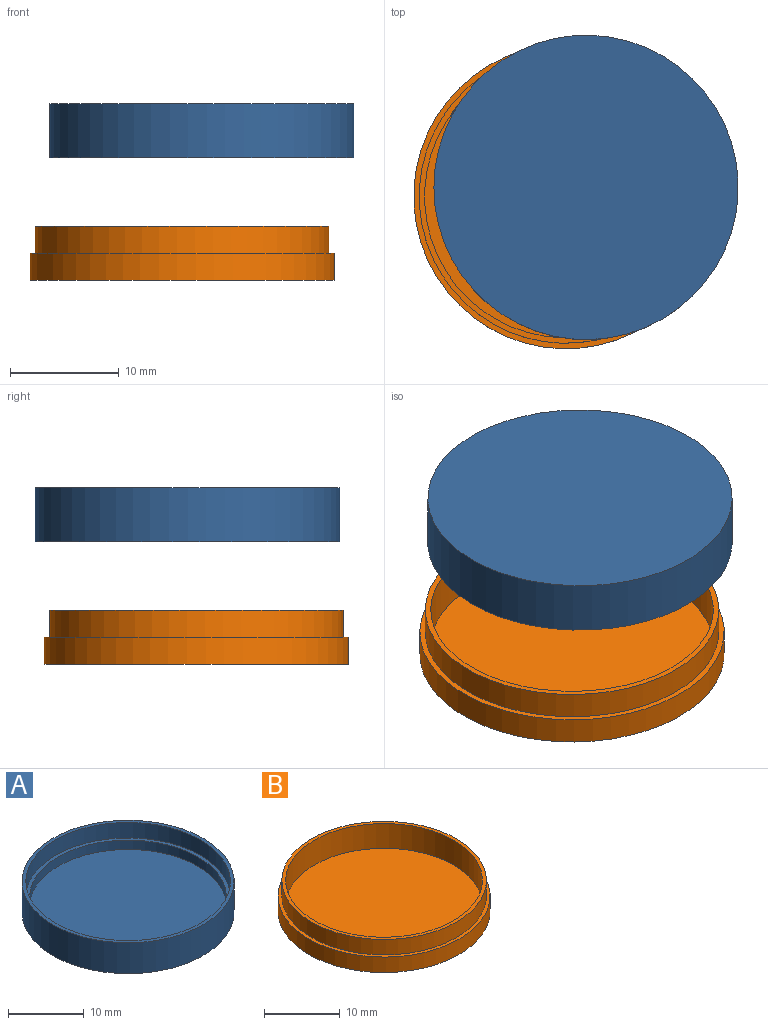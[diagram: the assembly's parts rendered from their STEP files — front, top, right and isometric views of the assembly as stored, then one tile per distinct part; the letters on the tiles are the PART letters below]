
ASSEMBLY  parts=2 mates=1
PART A: 7 faces, bbox 28x28x5 mm
  f0: plane 27x27mm, normal (0,0,1), area 41.6mm2, adj f2,f3
  f1: plane 26x26mm, normal (0,0,1), area 530.9mm2, adj f2
  f2: cylinder r=13mm len=26mm, axis (0,0,-1), area 122.5mm2, adj f0,f1
  f3: cylinder r=13.5mm len=27mm, axis (0,0,-1), area 212.1mm2, adj f0,f4
  f4: plane 28x28mm, normal (0,0,1), area 43.2mm2, adj f3,f6
  f5: plane 28x28mm, normal (0,0,-1), area 615.8mm2, adj f6
  f6: cylinder r=14mm len=28mm, axis (0,0,-1), area 439.8mm2, adj f4,f5
PART B: 7 faces, bbox 28x28x5 mm
  f0: plane 27x27mm, normal (0,0,1), area 41.6mm2, adj f2,f3
  f1: plane 26x26mm, normal (0,0,1), area 530.9mm2, adj f2
  f2: cylinder r=13mm len=26mm, axis (0,0,-1), area 326.7mm2, adj f0,f1
  f3: cylinder r=13.5mm len=27mm, axis (0,0,1), area 212.1mm2, adj f0,f4
  f4: plane 28x28mm, normal (0,0,1), area 43.2mm2, adj f3,f6
  f5: plane 28x28mm, normal (0,0,-1), area 615.8mm2, adj f6
  f6: cylinder r=14mm len=28mm, axis (0,0,-1), area 219.9mm2, adj f4,f5
PLACE A rot(axis=(0,1,0),180deg) t=(1.73,0.79,13.83)mm
PLACE B t=(-0.12,-0.03,-2.45)mm
MATE parallel A.f6 <-> B.f6  axis (0,0,1) through (1.73,0.79,11.33)mm
